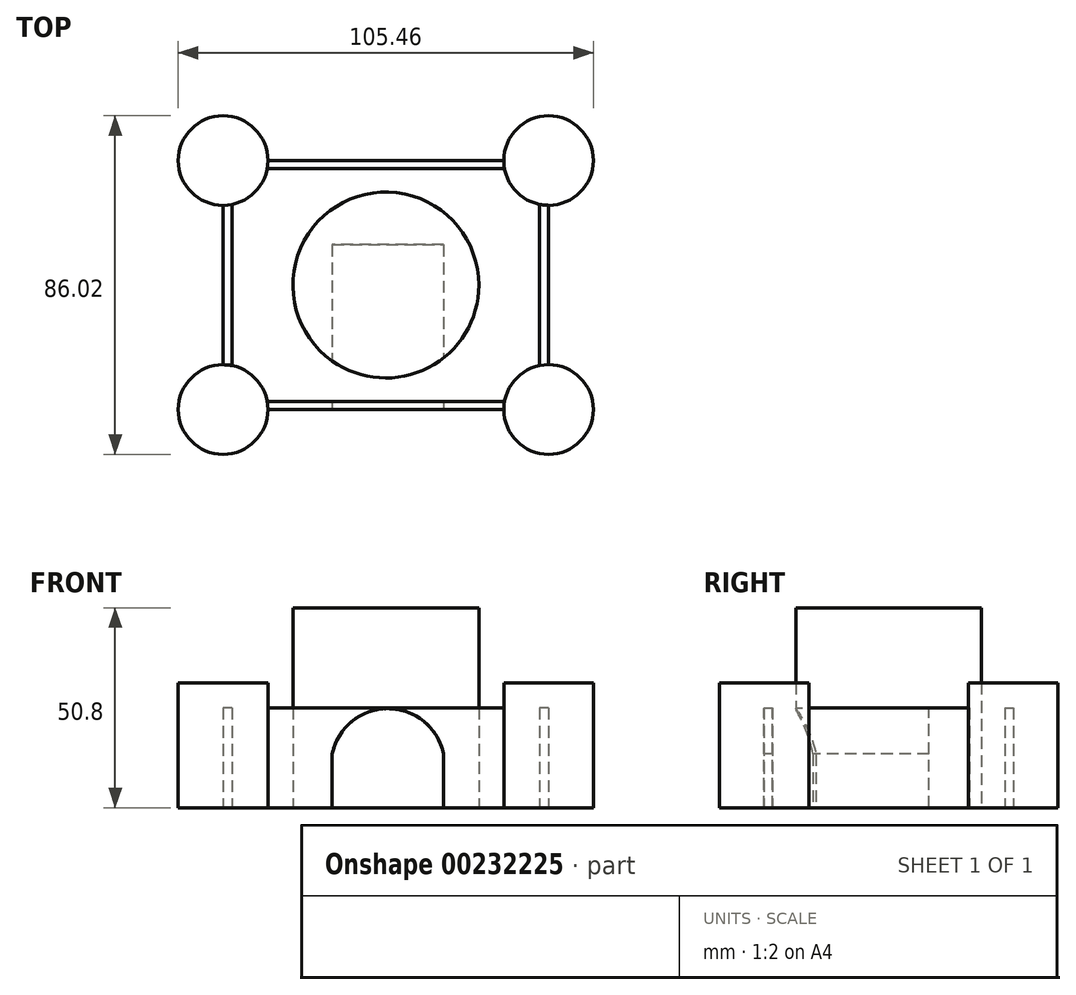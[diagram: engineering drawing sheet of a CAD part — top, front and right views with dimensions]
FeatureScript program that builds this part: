
annotation { "Feature Type Name" : "Feature", "Feature Type Description" : "" }
export const myFeature = defineFeature(function(context is Context, id is Id, definition is map)
    precondition{}
    {
        {
            var Q0;
            Q0=qCreatedBy(makeId("Top.planeOp"),FACE);
            var sketch = newSketch(context, id + "F0", { "sketchPlane" : qUnion([Q0])});
            skLineSegment(sketch, "E0.bottom", {"start": v(-29.97, -31.63) * mm, "end": v(29.97, -31.63) * mm});
            skLineSegment(sketch, "E0.top", {"start": v(-29.97, 31.63) * mm, "end": v(29.97, 31.63) * mm});
            skLineSegment(sketch, "E0.left", {"start": v(-41.35, -20.26) * mm, "end": v(-41.35, 20.26) * mm});
            skLineSegment(sketch, "E0.right", {"start": v(41.35, -20.26) * mm, "end": v(41.35, 20.26) * mm});
            skPoint(sketch, "E0.middle", {"position": v(0, 0) * mm});
            skCircle(sketch, "E1", {"center": v(0, 0) * mm, "radius": 23.61 * mm});
            skCircle(sketch, "E2", {"center": v(-41.35, 31.63) * mm, "radius": 11.38 * mm});
            skCircle(sketch, "E3", {"center": v(-41.35, -31.63) * mm, "radius": 11.38 * mm});
            skCircle(sketch, "E4", {"center": v(41.35, -31.63) * mm, "radius": 11.38 * mm});
            skCircle(sketch, "E5", {"center": v(41.35, 31.63) * mm, "radius": 11.38 * mm});
            skLineSegment(sketch, "E6.bottom", {"start": v(30.16, -29.56) * mm, "end": v(-30.16, -29.56) * mm});
            skLineSegment(sketch, "E6.top", {"start": v(30.16, 29.56) * mm, "end": v(-30.16, 29.56) * mm});
            skLineSegment(sketch, "E6.left", {"start": v(39.07, -20.48) * mm, "end": v(39.07, 20.48) * mm});
            skLineSegment(sketch, "E6.right", {"start": v(-39.07, -20.48) * mm, "end": v(-39.07, 20.48) * mm});
            skPoint(sketch, "E7.orphan", {"position": v(-39.07, -29.56) * mm});
            skPoint(sketch, "E8.orphan", {"position": v(39.07, -29.56) * mm});
            skPoint(sketch, "E9.orphan", {"position": v(39.07, 29.56) * mm});
            skPoint(sketch, "E10.orphan", {"position": v(-39.07, 29.56) * mm});
            skSolve(sketch);
        }
        {
            var Q0;
            {var subQ0=sQuery(id+"F0.wireOp",EDGE,"E0.top");Q0=makeQuery(id+"F0.imprint","IMPRINT",FACE,{"disambiguationData":[TD([[makeQuery(id+"F0.imprint","IMPRINT",EDGE,{"derivedFrom":subQ0}),-1.0]])]});}
            var Q1;
            {var subQ0=sQuery(id+"F0.wireOp",EDGE,"E0.left");Q1=makeQuery(id+"F0.imprint","IMPRINT",FACE,{"disambiguationData":[TD([[makeQuery(id+"F0.imprint","IMPRINT",EDGE,{"derivedFrom":subQ0}),-1.0]])]});}
            var Q2;
            {var subQ0=sQuery(id+"F0.wireOp",EDGE,"E0.bottom");Q2=makeQuery(id+"F0.imprint","IMPRINT",FACE,{"disambiguationData":[TD([[makeQuery(id+"F0.imprint","IMPRINT",EDGE,{"derivedFrom":subQ0}),1.0]])]});}
            var Q3;
            {var subQ0=sQuery(id+"F0.wireOp",EDGE,"E0.right");Q3=makeQuery(id+"F0.imprint","IMPRINT",FACE,{"disambiguationData":[TD([[makeQuery(id+"F0.imprint","IMPRINT",EDGE,{"derivedFrom":subQ0}),1.0]])]});}
            extrude(context, id + "F1", {"entities" : qUnion([Q0, Q1, Q2, Q3]), "depth" : 25.4 * mm});
        }
        {
            var Q0;
            {var subQ0=sQuery(id+"F0.wireOp",EDGE,"E2");var subQ1=makeQuery(id+"F0.imprint","INTERSECT",VERTEX,{"derivedFrom":[sQuery(id+"F0.wireOp",EDGE,"E0.top"),subQ0]});Q0=makeQuery(id+"F0.imprint","IMPRINT",FACE,{"disambiguationData":[TD([[makeQuery(id+"F0.imprint","IMPRINT",EDGE,{"disambiguationData":[TD([[subQ1,-1.0]])],"derivedFrom":subQ0}),1.0]])]});}
            var Q1;
            {var subQ0=sQuery(id+"F0.wireOp",EDGE,"E3");var subQ1=makeQuery(id+"F0.imprint","INTERSECT",VERTEX,{"derivedFrom":[sQuery(id+"F0.wireOp",EDGE,"E0.bottom"),subQ0]});Q1=makeQuery(id+"F0.imprint","IMPRINT",FACE,{"disambiguationData":[TD([[makeQuery(id+"F0.imprint","IMPRINT",EDGE,{"disambiguationData":[TD([[subQ1,-1.0]])],"derivedFrom":subQ0}),1.0]])]});}
            var Q2;
            {var subQ0=sQuery(id+"F0.wireOp",EDGE,"E4");var subQ1=makeQuery(id+"F0.imprint","INTERSECT",VERTEX,{"derivedFrom":[sQuery(id+"F0.wireOp",EDGE,"E0.right"),subQ0]});Q2=makeQuery(id+"F0.imprint","IMPRINT",FACE,{"disambiguationData":[TD([[makeQuery(id+"F0.imprint","IMPRINT",EDGE,{"disambiguationData":[TD([[subQ1,-1.0]])],"derivedFrom":subQ0}),1.0]])]});}
            var Q3;
            {var subQ0=sQuery(id+"F0.wireOp",EDGE,"E5");var subQ1=makeQuery(id+"F0.imprint","INTERSECT",VERTEX,{"derivedFrom":[sQuery(id+"F0.wireOp",EDGE,"E0.top"),subQ0]});Q3=makeQuery(id+"F0.imprint","IMPRINT",FACE,{"disambiguationData":[TD([[makeQuery(id+"F0.imprint","IMPRINT",EDGE,{"disambiguationData":[TD([[subQ1,-1.0]])],"derivedFrom":subQ0}),1.0]])]});}
            extrude(context, id + "F2", {"entities" : qUnion([Q0, Q1, Q2, Q3]), "depth" : 31.75 * mm});
        }
        {
            var Q0;
            Q0=makeQuery(id+"F0.imprint","IMPRINT",FACE,{"disambiguationData":[TD([[makeQuery(id+"F0.imprint","IMPRINT",EDGE,{"derivedFrom":sQuery(id+"F0.wireOp",EDGE,"E1")}),1.0]])]});
            extrude(context, id + "F3", {"entities" : qUnion([Q0]), "depth" : 50.8 * mm});
        }
        {
            var Q0;
            Q0=makeQuery(id+"F1.opExtrude","SWEPT_FACE",FACE,{"disambiguationData":[OSD([sQuery(id+"F0.wireOp",EDGE,"E0.bottom")])]});
            var sketch = newSketch(context, id + "F4", { "sketchPlane" : qUnion([Q0])});
            skLineSegment(sketch, "E11.bottom", {"start": v(-13.65, 0) * mm, "end": v(14.68, 0) * mm});
            skLineSegment(sketch, "E11.left", {"start": v(-13.65, 0) * mm, "end": v(-13.65, 13.65) * mm});
            skLineSegment(sketch, "E11.right", {"start": v(14.68, 0) * mm, "end": v(14.68, 13.65) * mm});
            skArc(sketch, "E12", {"start": v(14.68, 13.65) * mm, "mid": v(0.52, 25.18) * mm, "end": v(-13.65, 13.65) * mm});
            skSolve(sketch);
        }
        {
            var Q0;
            Q0=makeQuery(id+"F4.imprint","IMPRINT",FACE,{"disambiguationData":[TD([[makeQuery(id+"F4.imprint","IMPRINT",EDGE,{"derivedFrom":sQuery(id+"F4.wireOp",EDGE,"E11.bottom")}),1.0]])]});
            extrude(context, id + "F5", {"entities" : qUnion([Q0]), "operationType" : NewBodyOperationType.REMOVE, "oppositeDirection" : true, "depth" : 41.9 * mm});
        }
    });
